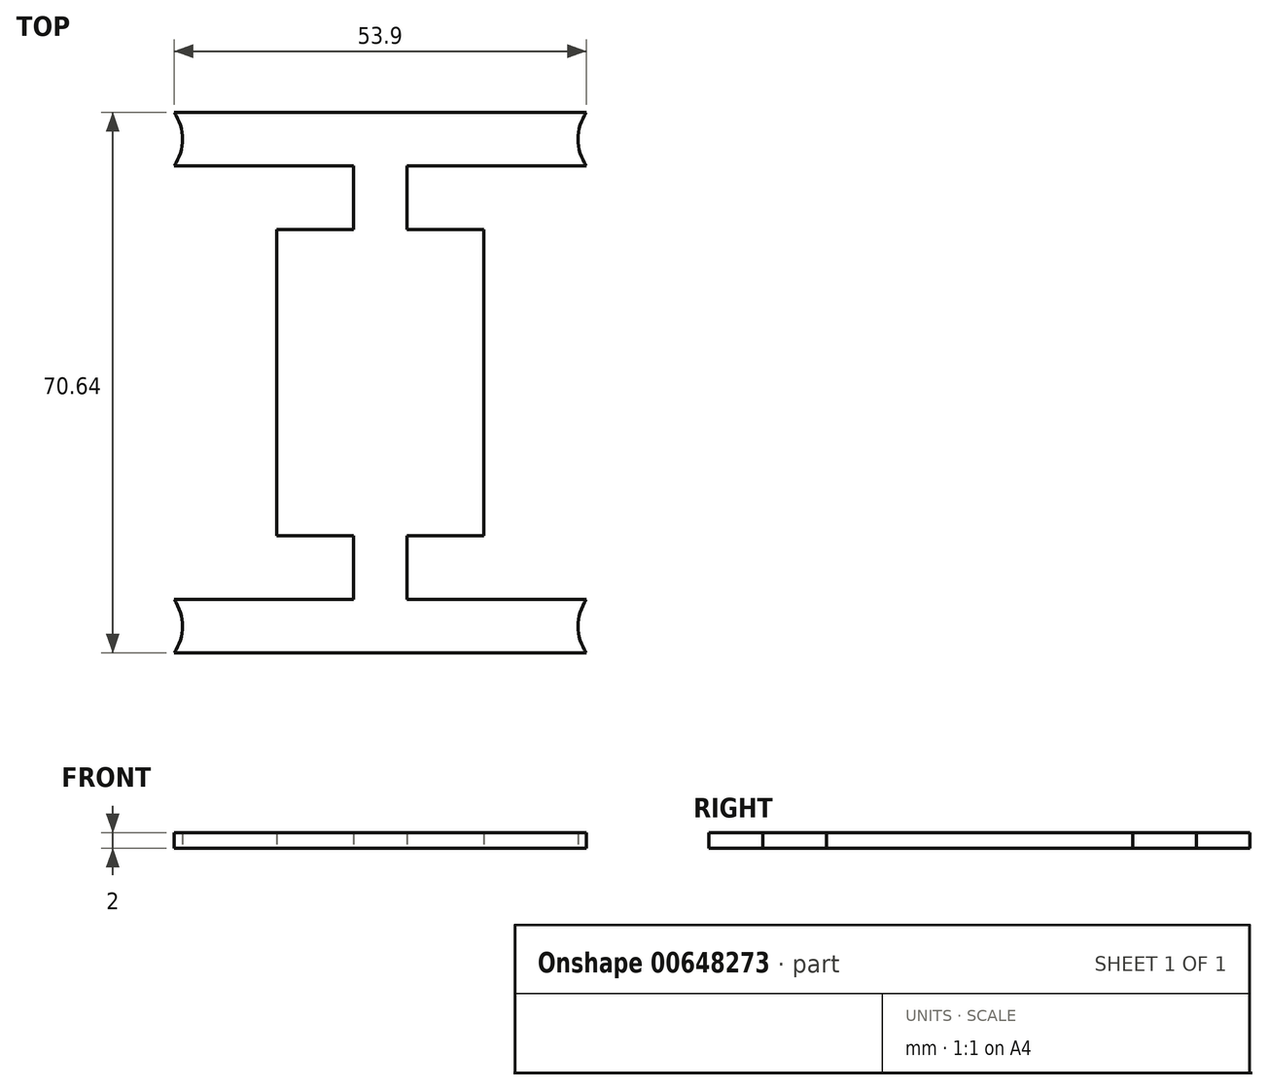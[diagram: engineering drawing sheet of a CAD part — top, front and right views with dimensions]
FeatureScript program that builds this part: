
annotation { "Feature Type Name" : "Feature", "Feature Type Description" : "" }
export const myFeature = defineFeature(function(context is Context, id is Id, definition is map)
    precondition{}
    {
        {
            var Q0;
            Q0=qCreatedBy(makeId("Top.planeOp"),FACE);
            var sketch = newSketch(context, id + "F0", { "sketchPlane" : qUnion([Q0])});
            skLineSegment(sketch, "E0.bottom", {"start": v(31.82, -31.82) * mm, "end": v(-31.82, -31.82) * mm, "construction": true});
            skLineSegment(sketch, "E0.top", {"start": v(31.82, 31.82) * mm, "end": v(-31.82, 31.82) * mm, "construction": true});
            skLineSegment(sketch, "E0.left", {"start": v(31.82, -31.82) * mm, "end": v(31.82, 31.82) * mm, "construction": true});
            skLineSegment(sketch, "E0.right", {"start": v(-31.82, -31.82) * mm, "end": v(-31.82, 31.82) * mm, "construction": true});
            skPoint(sketch, "E0.middle", {"position": v(0, 0) * mm});
            skCircle(sketch, "E1", {"center": v(-31.82, 31.82) * mm, "radius": 3.5 * mm});
            skCircle(sketch, "E2", {"center": v(31.82, 31.82) * mm, "radius": 3.5 * mm});
            skCircle(sketch, "E3", {"center": v(-31.82, -31.82) * mm, "radius": 3.5 * mm});
            skCircle(sketch, "E4", {"center": v(31.82, -31.82) * mm, "radius": 3.5 * mm});
            skCircle(sketch, "E5", {"center": v(31.82, 31.82) * mm, "radius": 6 * mm});
            skCircle(sketch, "E6", {"center": v(-31.82, 31.82) * mm, "radius": 6 * mm});
            skCircle(sketch, "E7", {"center": v(-31.82, -31.82) * mm, "radius": 6 * mm});
            skCircle(sketch, "E8", {"center": v(31.82, -31.82) * mm, "radius": 6 * mm});
            skLineSegment(sketch, "E9.bottom", {"start": v(13.5, -20) * mm, "end": v(-13.5, -20) * mm});
            skLineSegment(sketch, "E9.top", {"start": v(13.5, 20) * mm, "end": v(-13.5, 20) * mm});
            skLineSegment(sketch, "E9.left", {"start": v(13.5, -20) * mm, "end": v(13.5, 20) * mm});
            skLineSegment(sketch, "E9.right", {"start": v(-13.5, -20) * mm, "end": v(-13.5, 20) * mm});
            skLineSegment(sketch, "E10", {"start": v(-26.95, 35.32) * mm, "end": v(26.95, 35.32) * mm});
            skLineSegment(sketch, "E11", {"start": v(-26.95, 28.32) * mm, "end": v(-3.5, 28.32) * mm});
            skLineSegment(sketch, "E12", {"start": v(-3.5, 28.32) * mm, "end": v(-3.5, 20) * mm});
            skLineSegment(sketch, "E13", {"start": v(-26.95, -35.32) * mm, "end": v(26.95, -35.32) * mm});
            skLineSegment(sketch, "E14", {"start": v(-26.95, -28.32) * mm, "end": v(-3.5, -28.32) * mm});
            skLineSegment(sketch, "E15", {"start": v(-3.5, -28.32) * mm, "end": v(-3.5, -20) * mm});
            skLineSegment(sketch, "E16", {"start": v(0, 35.32) * mm, "end": v(0, -52.14) * mm, "construction": true});
            skLineSegment(sketch, "E17.MirrorCS", {"start": v(26.95, 28.32) * mm, "end": v(3.5, 28.32) * mm});
            skLineSegment(sketch, "E18.MirrorCS", {"start": v(3.5, 28.32) * mm, "end": v(3.5, 20) * mm});
            skLineSegment(sketch, "E19.MirrorCS", {"start": v(26.95, -28.32) * mm, "end": v(3.5, -28.32) * mm});
            skLineSegment(sketch, "E20.MirrorCS", {"start": v(3.5, -28.32) * mm, "end": v(3.5, -20) * mm});
            skSolve(sketch);
        }
        {
            var Q0;
            {var subQ0=sQuery(id+"F0.wireOp",EDGE,"E9.left");Q0=makeQuery(id+"F0.imprint","IMPRINT",FACE,{"disambiguationData":[TD([[makeQuery(id+"F0.imprint","IMPRINT",EDGE,{"derivedFrom":subQ0}),1.0]])]});}
            var Q1;
            {var subQ0=sQuery(id+"F0.wireOp",EDGE,"E13");Q1=makeQuery(id+"F0.imprint","IMPRINT",FACE,{"disambiguationData":[TD([[makeQuery(id+"F0.imprint","IMPRINT",EDGE,{"derivedFrom":subQ0}),1.0]])]});}
            var Q2;
            {var subQ0=sQuery(id+"F0.wireOp",EDGE,"E10");Q2=makeQuery(id+"F0.imprint","IMPRINT",FACE,{"disambiguationData":[TD([[makeQuery(id+"F0.imprint","IMPRINT",EDGE,{"derivedFrom":subQ0}),-1.0]])]});}
            extrude(context, id + "F1", {"entities" : qUnion([Q0, Q1, Q2]), "depth" : 2 * mm, "offsetDistance" : 25 * mm});
        }
    });
